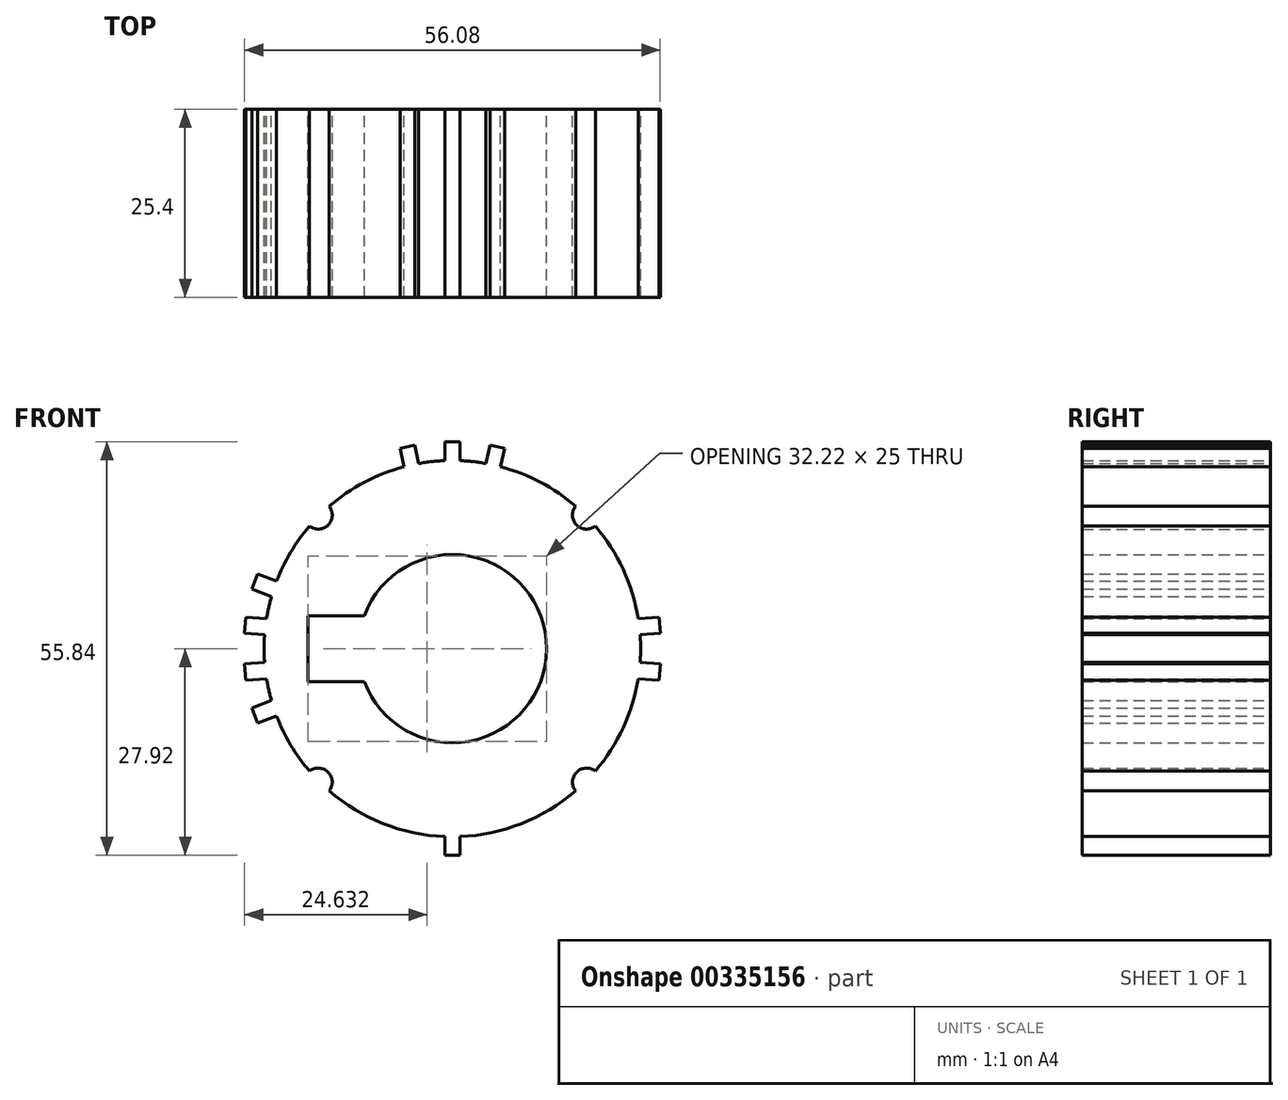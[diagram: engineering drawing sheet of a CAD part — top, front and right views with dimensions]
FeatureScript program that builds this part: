
annotation { "Feature Type Name" : "Feature", "Feature Type Description" : "" }
export const myFeature = defineFeature(function(context is Context, id is Id, definition is map)
    precondition{}
    {
        {
            var Q0;
            Q0=qCreatedBy(makeId("Front.planeOp"),FACE);
            var sketch = newSketch(context, id + "F0", { "sketchPlane" : qUnion([Q0])});
            skArc(sketch, "E0", {"start": v(16.62, 19.21) * mm, "mid": v(11.87, 22.46) * mm, "end": v(6.52, 24.55) * mm});
            skArc(sketch, "E1", {"start": v(-4.44, 11.9) * mm, "mid": v(-8.98, 8.98) * mm, "end": v(-11.9, 4.45) * mm});
            skArc(sketch, "E2", {"start": v(16.62, 19.21) * mm, "mid": v(16.76, 16.69) * mm, "end": v(19.28, 16.53) * mm});
            skPoint(sketch, "E3.end.orphan", {"position": v(0, 38.1) * mm});
            skPoint(sketch, "E4.end.orphan", {"position": v(38.1, 0) * mm});
            skArc(sketch, "E5.MirrorCS", {"start": v(-16.62, 19.21) * mm, "mid": v(-16.76, 16.69) * mm, "end": v(-19.28, 16.53) * mm});
            skArc(sketch, "E6.MirrorCS", {"start": v(16.62, -19.21) * mm, "mid": v(16.76, -16.69) * mm, "end": v(19.28, -16.53) * mm});
            skArc(sketch, "E7.MirrorCS", {"start": v(-16.62, -19.21) * mm, "mid": v(-16.76, -16.69) * mm, "end": v(-19.28, -16.53) * mm});
            skArc(sketch, "E8.trimOffspring", {"start": v(19.28, -16.53) * mm, "mid": v(23.04, -10.7) * mm, "end": v(25.07, -4.06) * mm});
            skArc(sketch, "E9.trimOffspring", {"start": v(-19.28, 16.53) * mm, "mid": v(-21.82, 13) * mm, "end": v(-23.71, 9.1) * mm});
            skArc(sketch, "E10.trimOffspring", {"start": v(-16.62, -19.21) * mm, "mid": v(-9.34, -23.62) * mm, "end": v(-1.02, -25.38) * mm});
            skLineSegment(sketch, "E11", {"start": v(1.02, 25.38) * mm, "end": v(1.02, 27.92) * mm});
            skLineSegment(sketch, "E12.MirrorCS", {"start": v(-1.02, 25.38) * mm, "end": v(-1.02, 27.92) * mm});
            skLineSegment(sketch, "E13", {"start": v(1.02, 27.92) * mm, "end": v(-1.02, 27.92) * mm});
            skArc(sketch, "E14.trimOffspring", {"start": v(-1.02, 25.38) * mm, "mid": v(-2.78, 25.25) * mm, "end": v(-4.53, 25) * mm});
            skLineSegment(sketch, "E15.MirrorCS", {"start": v(4.53, 25) * mm, "end": v(5.09, 27.47) * mm});
            skLineSegment(sketch, "E16.MirrorCS", {"start": v(5.09, 27.47) * mm, "end": v(7.07, 27.03) * mm});
            skLineSegment(sketch, "E17.MirrorCS", {"start": v(6.52, 24.55) * mm, "end": v(7.07, 27.03) * mm});
            skLineSegment(sketch, "E18.MirrorCS", {"start": v(-4.53, 25) * mm, "end": v(-5.09, 27.47) * mm});
            skLineSegment(sketch, "E19.MirrorCS", {"start": v(-6.52, 24.55) * mm, "end": v(-7.07, 27.03) * mm});
            skLineSegment(sketch, "E20.MirrorCS", {"start": v(-5.09, 27.47) * mm, "end": v(-7.07, 27.03) * mm});
            skArc(sketch, "E21.trimOffspring", {"start": v(4.53, 25) * mm, "mid": v(2.78, 25.25) * mm, "end": v(1.02, 25.38) * mm});
            skArc(sketch, "E22.trimOffspring", {"start": v(-6.52, 24.55) * mm, "mid": v(-11.87, 22.46) * mm, "end": v(-16.62, 19.21) * mm});
            skLineSegment(sketch, "E23.MirrorCS", {"start": v(1.02, -25.38) * mm, "end": v(1.02, -27.92) * mm});
            skLineSegment(sketch, "E24.MirrorCS", {"start": v(1.02, -27.92) * mm, "end": v(-1.02, -27.92) * mm});
            skLineSegment(sketch, "E25.MirrorCS", {"start": v(-1.02, -25.38) * mm, "end": v(-1.02, -27.92) * mm});
            skArc(sketch, "E26.trimOffspring", {"start": v(1.02, -25.38) * mm, "mid": v(9.34, -23.62) * mm, "end": v(16.62, -19.21) * mm});
            skLineSegment(sketch, "E27", {"start": v(28.04, -2.06) * mm, "end": v(27.88, -4.26) * mm});
            skLineSegment(sketch, "E28", {"start": v(27.88, -4.26) * mm, "end": v(25.07, -4.06) * mm});
            skLineSegment(sketch, "E29.trimOffspring", {"start": v(25.33, -1.86) * mm, "end": v(28.04, -2.06) * mm});
            skArc(sketch, "E30.trimOffspring", {"start": v(25.33, -1.86) * mm, "mid": v(25.4, 0) * mm, "end": v(25.33, 1.86) * mm});
            skLineSegment(sketch, "E31.MirrorCS", {"start": v(25.33, 1.86) * mm, "end": v(28.04, 2.06) * mm});
            skLineSegment(sketch, "E32.MirrorCS", {"start": v(28.04, 2.06) * mm, "end": v(27.88, 4.26) * mm});
            skLineSegment(sketch, "E33.MirrorCS", {"start": v(27.88, 4.26) * mm, "end": v(25.07, 4.06) * mm});
            skArc(sketch, "E34.trimOffspring", {"start": v(25.07, 4.06) * mm, "mid": v(23.04, 10.7) * mm, "end": v(19.28, 16.53) * mm});
            skLineSegment(sketch, "E35.MirrorCS", {"start": v(-27.88, -4.26) * mm, "end": v(-25.07, -4.06) * mm});
            skLineSegment(sketch, "E36.MirrorCS", {"start": v(-28.04, -2.06) * mm, "end": v(-27.88, -4.26) * mm});
            skLineSegment(sketch, "E37.MirrorCS", {"start": v(-25.33, -1.86) * mm, "end": v(-28.04, -2.06) * mm});
            skLineSegment(sketch, "E38.MirrorCS", {"start": v(-25.33, 1.86) * mm, "end": v(-28.04, 2.06) * mm});
            skLineSegment(sketch, "E39.MirrorCS", {"start": v(-28.04, 2.06) * mm, "end": v(-27.88, 4.26) * mm});
            skLineSegment(sketch, "E40.MirrorCS", {"start": v(-27.88, 4.26) * mm, "end": v(-25.07, 4.06) * mm});
            skLineSegment(sketch, "E41.MirrorCS", {"start": v(-27.04, -8.02) * mm, "end": v(-24.41, -7.01) * mm});
            skLineSegment(sketch, "E42.MirrorCS", {"start": v(-26.25, -10.08) * mm, "end": v(-27.04, -8.02) * mm});
            skLineSegment(sketch, "E43.MirrorCS", {"start": v(-23.71, -9.1) * mm, "end": v(-26.25, -10.08) * mm});
            skArc(sketch, "E44.trimOffspring", {"start": v(-23.71, -9.1) * mm, "mid": v(-21.82, -13) * mm, "end": v(-19.28, -16.53) * mm});
            skArc(sketch, "E45.trimOffspring", {"start": v(-25.07, -4.06) * mm, "mid": v(-24.79, -5.54) * mm, "end": v(-24.41, -7.01) * mm});
            skArc(sketch, "E46.trimOffspring", {"start": v(-25.33, 1.86) * mm, "mid": v(-25.4, 0) * mm, "end": v(-25.33, -1.86) * mm});
            skLineSegment(sketch, "E47.MirrorCS", {"start": v(-27.04, 8.02) * mm, "end": v(-24.41, 7.01) * mm});
            skLineSegment(sketch, "E48.MirrorCS", {"start": v(-26.25, 10.08) * mm, "end": v(-27.04, 8.02) * mm});
            skLineSegment(sketch, "E49.MirrorCS", {"start": v(-23.71, 9.1) * mm, "end": v(-26.25, 10.08) * mm});
            skArc(sketch, "E50.trimOffspring", {"start": v(-24.41, 7.01) * mm, "mid": v(-24.79, 5.54) * mm, "end": v(-25.07, 4.06) * mm});
            skLineSegment(sketch, "E51.MirrorCS", {"start": v(-19.52, 4.45) * mm, "end": v(-19.52, -4.44) * mm});
            skLineSegment(sketch, "E52.MirrorCS", {"start": v(-11.9, -4.44) * mm, "end": v(-19.52, -4.44) * mm});
            skLineSegment(sketch, "E53.MirrorCS", {"start": v(-11.9, 4.45) * mm, "end": v(-19.52, 4.45) * mm});
            skPoint(sketch, "E54.end.orphan", {"position": v(-38.1, 0) * mm});
            skArc(sketch, "E55", {"start": v(-11.9, -4.44) * mm, "mid": v(12.7, 0) * mm, "end": v(-11.9, 4.45) * mm});
            skPoint(sketch, "E56.MirrorCS.end.orphan", {"position": v(4.45, 19.52) * mm});
            skPoint(sketch, "E57.end.orphan", {"position": v(-4.44, 19.52) * mm});
            skArc(sketch, "E58.trimOffspring", {"start": v(-11.9, -4.44) * mm, "mid": v(8.98, -8.98) * mm, "end": v(4.45, 11.9) * mm});
            skSolve(sketch);
        }
        {
            var Q0;
            Q0=qSketchRegion(id+"F0",true);
            extrude(context, id + "F1", {"entities" : qUnion([Q0]), "depth" : 25.4 * mm, "offsetDistance" : 25.4 * mm});
        }
    });
